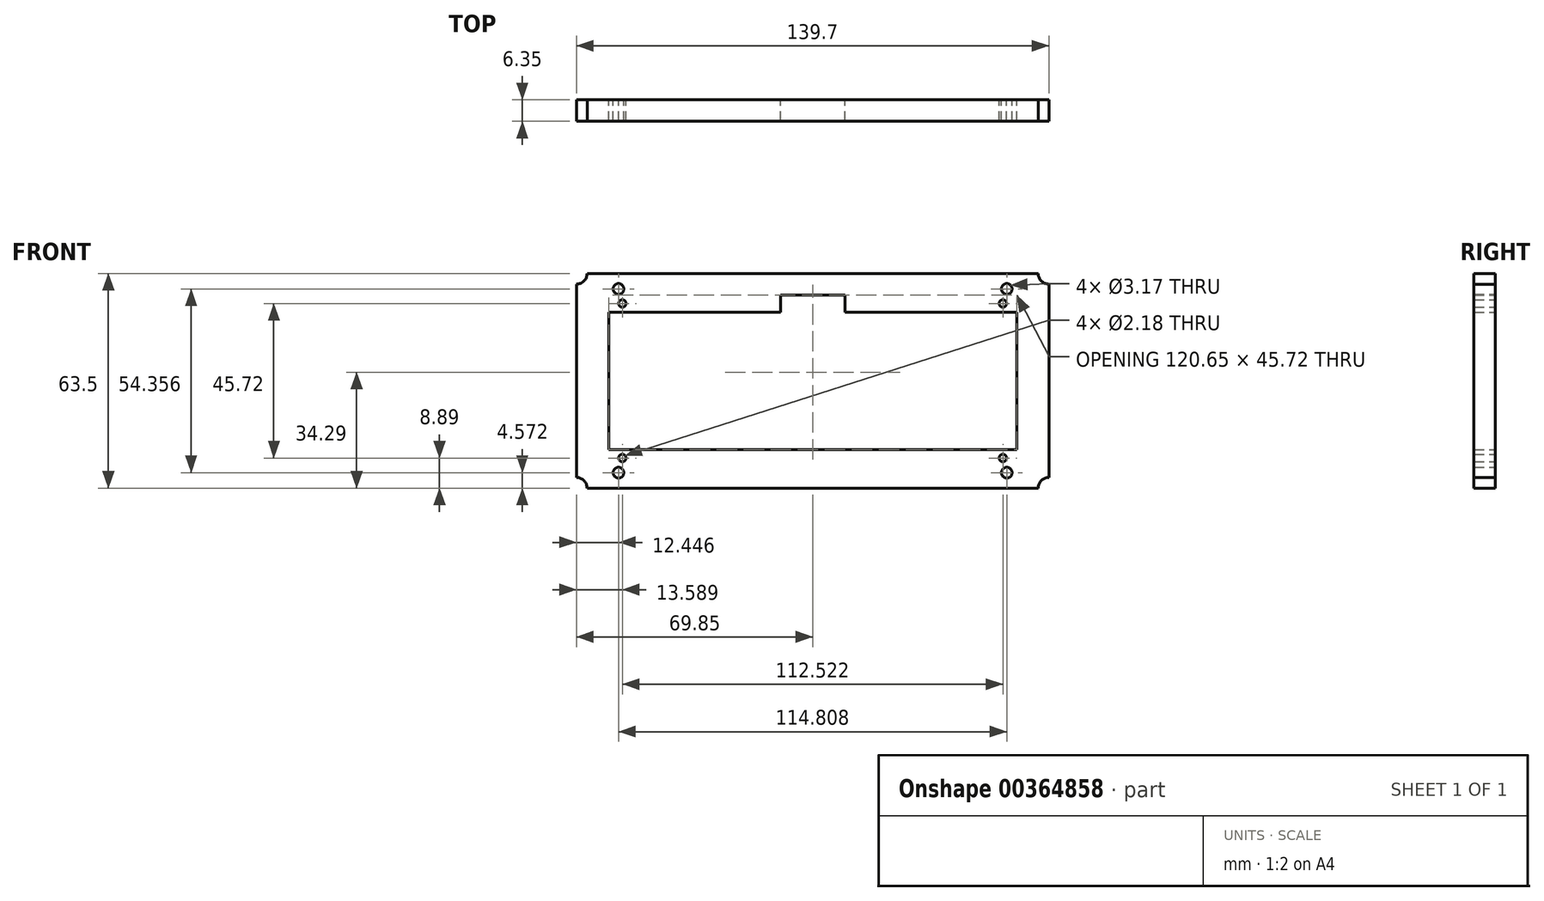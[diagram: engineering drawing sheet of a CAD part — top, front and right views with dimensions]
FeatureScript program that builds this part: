
annotation { "Feature Type Name" : "Feature", "Feature Type Description" : "" }
export const myFeature = defineFeature(function(context is Context, id is Id, definition is map)
    precondition{}
    {
        {
            var Q0;
            Q0=qCreatedBy(makeId("Front.planeOp"),FACE);
            var sketch = newSketch(context, id + "F0", { "sketchPlane" : qUnion([Q0])});
            skLineSegment(sketch, "E0.bottom", {"start": v(-66.68, 31.75) * mm, "end": v(66.68, 31.75) * mm});
            skLineSegment(sketch, "E0.top", {"start": v(-66.68, -31.75) * mm, "end": v(66.68, -31.75) * mm});
            skLineSegment(sketch, "E0.left", {"start": v(-69.85, 28.57) * mm, "end": v(-69.85, -28.58) * mm});
            skLineSegment(sketch, "E0.right", {"start": v(69.85, 28.57) * mm, "end": v(69.85, -28.58) * mm});
            skPoint(sketch, "E0.middle", {"position": v(0, 0) * mm});
            skLineSegment(sketch, "E1.bottom", {"start": v(-60.33, 20.32) * mm, "end": v(60.33, 20.32) * mm});
            skLineSegment(sketch, "E1.top", {"start": v(-60.33, -20.32) * mm, "end": v(60.33, -20.32) * mm});
            skLineSegment(sketch, "E1.left", {"start": v(-60.33, 20.32) * mm, "end": v(-60.33, -20.32) * mm});
            skLineSegment(sketch, "E1.right", {"start": v(60.33, 20.32) * mm, "end": v(60.33, -20.32) * mm});
            skLineSegment(sketch, "E2.bottom", {"start": v(-57.4, 27.18) * mm, "end": v(57.4, 27.18) * mm, "construction": true});
            skLineSegment(sketch, "E2.top", {"start": v(-57.4, -27.18) * mm, "end": v(57.4, -27.18) * mm, "construction": true});
            skLineSegment(sketch, "E2.left", {"start": v(-57.4, 27.18) * mm, "end": v(-57.4, -27.18) * mm, "construction": true});
            skLineSegment(sketch, "E2.right", {"start": v(57.4, 27.18) * mm, "end": v(57.4, -27.18) * mm, "construction": true});
            skLineSegment(sketch, "E3.bottom", {"start": v(-56.26, 22.86) * mm, "end": v(56.26, 22.86) * mm, "construction": true});
            skLineSegment(sketch, "E3.top", {"start": v(-56.26, -22.86) * mm, "end": v(56.26, -22.86) * mm, "construction": true});
            skLineSegment(sketch, "E3.left", {"start": v(-56.26, 22.86) * mm, "end": v(-56.26, -22.86) * mm, "construction": true});
            skLineSegment(sketch, "E3.right", {"start": v(56.26, 22.86) * mm, "end": v(56.26, -22.86) * mm, "construction": true});
            skCircle(sketch, "E4", {"center": v(-57.4, 27.18) * mm, "radius": 1.59 * mm});
            skCircle(sketch, "E5", {"center": v(57.4, -27.18) * mm, "radius": 1.59 * mm});
            skCircle(sketch, "E6", {"center": v(57.4, 27.18) * mm, "radius": 1.59 * mm});
            skCircle(sketch, "E7", {"center": v(-57.4, -27.18) * mm, "radius": 1.59 * mm});
            skCircle(sketch, "E8", {"center": v(-56.26, 22.86) * mm, "radius": 1.1 * mm});
            skCircle(sketch, "E9", {"center": v(56.26, 22.86) * mm, "radius": 1.1 * mm});
            skCircle(sketch, "E10", {"center": v(56.26, -22.86) * mm, "radius": 1.1 * mm});
            skCircle(sketch, "E11", {"center": v(-56.26, -22.86) * mm, "radius": 1.1 * mm});
            skArc(sketch, "E12", {"start": v(-69.85, 28.57) * mm, "mid": v(-67.6, 29.5) * mm, "end": v(-66.68, 31.75) * mm});
            skArc(sketch, "E13", {"start": v(-66.68, -31.75) * mm, "mid": v(-67.6, -29.5) * mm, "end": v(-69.85, -28.58) * mm});
            skArc(sketch, "E14", {"start": v(69.85, -28.58) * mm, "mid": v(67.6, -29.5) * mm, "end": v(66.68, -31.75) * mm});
            skArc(sketch, "E15", {"start": v(66.68, 31.75) * mm, "mid": v(67.6, 29.5) * mm, "end": v(69.85, 28.57) * mm});
            skLineSegment(sketch, "E16.bottom", {"start": v(9.53, 25.4) * mm, "end": v(-9.53, 25.4) * mm});
            skLineSegment(sketch, "E16.left", {"start": v(9.53, 25.4) * mm, "end": v(9.53, 20.32) * mm});
            skLineSegment(sketch, "E16.right", {"start": v(-9.53, 25.4) * mm, "end": v(-9.53, 20.32) * mm});
            skPoint(sketch, "E16.middle", {"position": v(0, 20.32) * mm});
            skLineSegment(sketch, "E17", {"start": v(-76.57, 0) * mm, "end": v(73.53, 0) * mm});
            skPoint(sketch, "E17.startSnap0", {"position": v(-69.85, 0) * mm});
            skLineSegment(sketch, "E18", {"start": v(9.53, 20.32) * mm, "end": v(-9.53, 20.32) * mm});
            skLineSegment(sketch, "E19.bottom", {"start": v(-9.53, 25.4) * mm, "end": v(9.53, 25.4) * mm});
            skLineSegment(sketch, "E19.top", {"start": v(-9.53, 20.32) * mm, "end": v(9.53, 20.32) * mm});
            skSolve(sketch);
        }
        {
            var Q0;
            Q0 = qSketchRegion(id + "F0", true);
            extrude(context, id + "F1", {"entities" : qUnion([Q0]), "depth" : 6.35 * mm});
        }
    });
